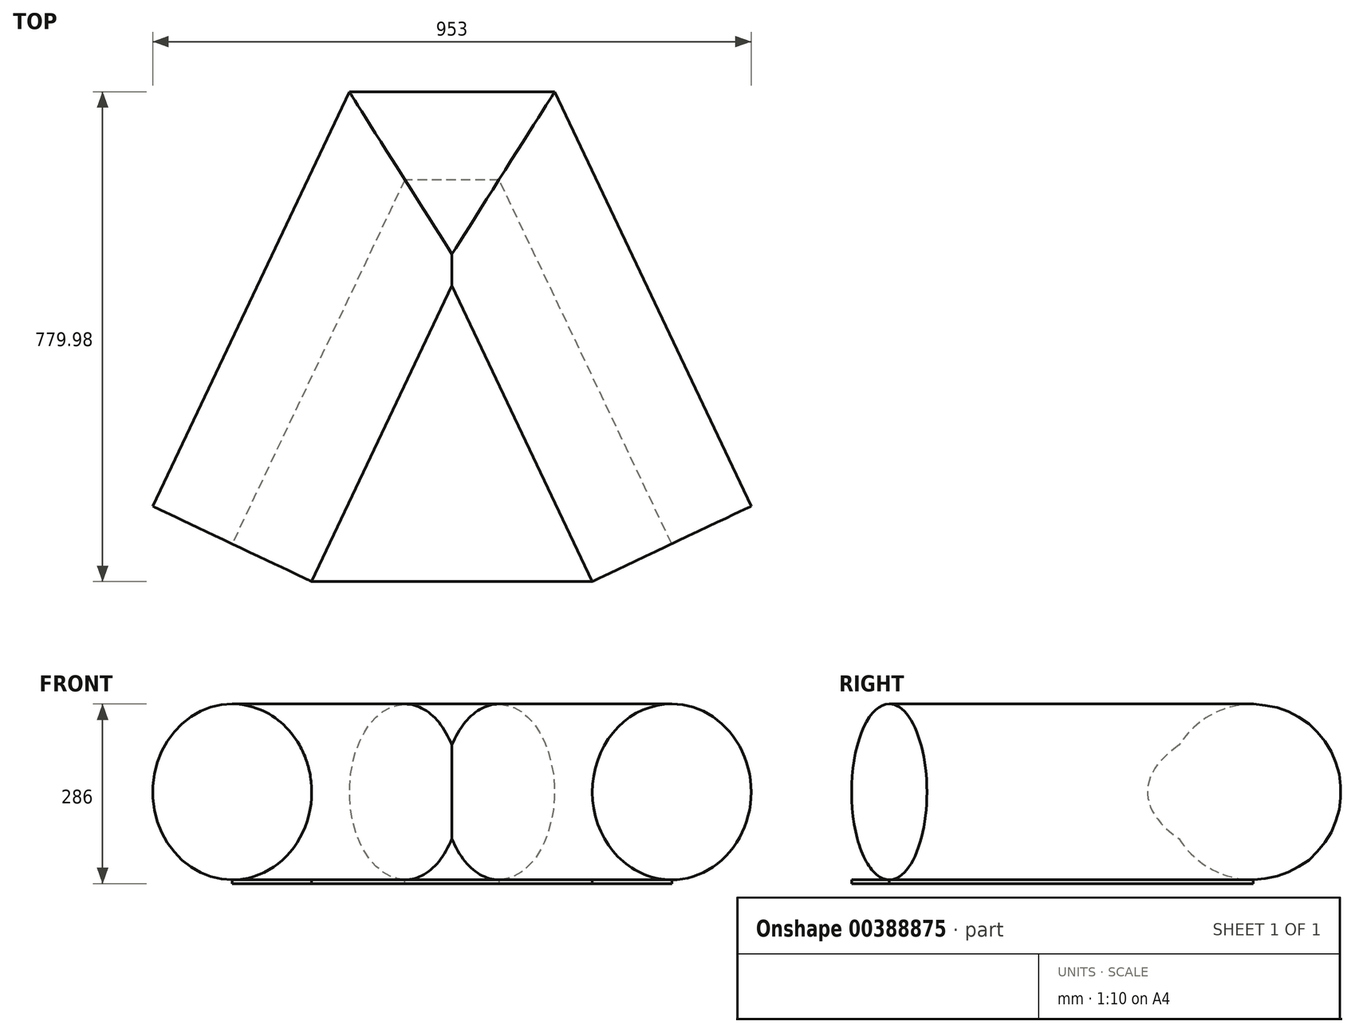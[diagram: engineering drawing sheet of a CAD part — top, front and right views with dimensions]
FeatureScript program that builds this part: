
annotation { "Feature Type Name" : "Feature", "Feature Type Description" : "" }
export const myFeature = defineFeature(function(context is Context, id is Id, definition is map)
    precondition{}
    {
        {
            var Q0;
            Q0=qCreatedBy(makeId("Top.planeOp"),FACE);
            var sketch = newSketch(context, id + "F0", { "sketchPlane" : qUnion([Q0])});
            skLineSegment(sketch, "E0", {"start": v(-75, 580) * mm, "end": v(75, 580) * mm});
            skLineSegment(sketch, "E1", {"start": v(75, 580) * mm, "end": v(350, 0) * mm});
            skLineSegment(sketch, "E2", {"start": v(-75, 580) * mm, "end": v(-350, 0) * mm});
            skSolve(sketch);
        }
        {
            var Q0;
            Q0=sQuery(id+"F0.wireOp",VERTEX,"E2.end");
            var Q1;
            Q1=sQuery(id+"F0.wireOp",EDGE,"E2");
            cPlane(context, id + "F1", {"entities" : qUnion([Q0, Q1]), "cplaneType" : CPlaneType.CURVE_POINT, "offset" : 25 * mm, "width" : 150 * mm, "height" : 150 * mm});
        }
        {
            var Q0;
            Q0=qCreatedBy(id+"F1.planeOp",FACE);
            var sketch = newSketch(context, id + "F2", { "sketchPlane" : qUnion([Q0])});
            skCircle(sketch, "E3", {"center": v(-316.25, 0) * mm, "radius": 140 * mm});
            skSolve(sketch);
        }
        {
            var Q0;
            Q0=makeQuery(id+"F2.imprint","IMPRINT",FACE,{"disambiguationData":[TD([[makeQuery(id+"F2.imprint","IMPRINT",EDGE,{"derivedFrom":sQuery(id+"F2.wireOp",EDGE,"E3")}),1.0]])]});
            var Q1;
            Q1=sQuery(id+"F0.wireOp",EDGE,"E2");
            var Q2;
            Q2=sQuery(id+"F0.wireOp",EDGE,"E0");
            sweep(context, id + "F3", {"profiles" : qUnion([Q0]), "path" : qUnion([Q1, Q2])});
        }
        {
            var Q0;
            Q0=sQuery(id+"F0.wireOp",EDGE,"E1");
            var Q1;
            Q1=sQuery(id+"F0.wireOp",VERTEX,"E1.end");
            cPlane(context, id + "F4", {"entities" : qUnion([Q0, Q1]), "cplaneType" : CPlaneType.CURVE_POINT, "offset" : 25 * mm, "width" : 150 * mm, "height" : 150 * mm});
        }
        {
            var Q0;
            Q0=qCreatedBy(id+"F4.planeOp",FACE);
            var sketch = newSketch(context, id + "F5", { "sketchPlane" : qUnion([Q0])});
            skCircle(sketch, "E4", {"center": v(316.25, 0) * mm, "radius": 140 * mm});
            skSolve(sketch);
        }
        {
            var Q0;
            Q0=makeQuery(id+"F5.imprint","IMPRINT",FACE,{"disambiguationData":[TD([[makeQuery(id+"F5.imprint","IMPRINT",EDGE,{"derivedFrom":sQuery(id+"F5.wireOp",EDGE,"E4")}),1.0]])]});
            var Q1;
            Q1=sQuery(id+"F0.wireOp",EDGE,"E1");
            var Q2;
            Q2=sQuery(id+"F0.wireOp",EDGE,"E0");
            sweep(context, id + "F6", {"operationType" : NewBodyOperationType.ADD, "profiles" : qUnion([Q0]), "path" : qUnion([Q1, Q2])});
        }
        {
            var Q0;
            Q0=qCreatedBy(makeId("Top.planeOp"),FACE);
            cPlane(context, id + "F7", {"entities" : qUnion([Q0]), "cplaneType" : CPlaneType.OFFSET, "offset" : 140 * mm, "oppositeDirection" : true, "width" : 150 * mm, "height" : 150 * mm});
        }
        {
            var Q0;
            Q0=qCreatedBy(id+"F7.planeOp",FACE);
            var sketch = newSketch(context, id + "F8", { "sketchPlane" : qUnion([Q0])});
            skLineSegment(sketch, "E5", {"start": v(0, 411.4) * mm, "end": v(-223.5, -59.98) * mm});
            skLineSegment(sketch, "E6", {"start": v(-476.5, 59.98) * mm, "end": v(-163.56, 720) * mm});
            skLineSegment(sketch, "E7.0", {"start": v(-223.5, -59.98) * mm, "end": v(-476.5, 59.98) * mm});
            skLineSegment(sketch, "E8.0", {"start": v(223.5, -59.98) * mm, "end": v(476.5, 59.98) * mm});
            skLineSegment(sketch, "E9", {"start": v(223.5, -59.98) * mm, "end": v(0, 411.4) * mm});
            skLineSegment(sketch, "E10", {"start": v(-350, 0) * mm, "end": v(-223.5, -59.98) * mm});
            skLineSegment(sketch, "E11", {"start": v(-223.5, -59.98) * mm, "end": v(223.5, -59.98) * mm});
            skLineSegment(sketch, "E12", {"start": v(350, 0) * mm, "end": v(75.17, 579.63) * mm});
            skLineSegment(sketch, "E13", {"start": v(75.17, 579.63) * mm, "end": v(-75.17, 579.63) * mm});
            skLineSegment(sketch, "E14", {"start": v(-75.17, 579.63) * mm, "end": v(-350, 0) * mm});
            skSolve(sketch);
        }
        {
            var Q0;
            Q0=makeQuery(id+"F8.imprint","IMPRINT",FACE,{"disambiguationData":[TD([[makeQuery(id+"F8.imprint","IMPRINT",EDGE,{"derivedFrom":sQuery(id+"F8.wireOp",EDGE,"E5")}),-1.0]])]});
            var Q1;
            Q1=makeQuery(id+"F8.imprint","IMPRINT",FACE,{"disambiguationData":[TD([[makeQuery(id+"F8.imprint","IMPRINT",EDGE,{"derivedFrom":sQuery(id+"F8.wireOp",EDGE,"E5")}),1.0]])]});
            extrude(context, id + "F9", {"entities" : qUnion([Q0, Q1]), "oppositeDirection" : true, "depth" : 6 * mm});
        }
    });
